# Revit family: Table-Teknion-CWRB_Reception_Communal_Bar-R2016
name_source: partatom
category: Furniture
revit_build: Autodesk Revit 2018 (Build: 20190510_1515(x64)
units: mm (PartAtom-declared; Revit-internal decimal feet)

## family parameters
Always vertical = Yes
Cut with Voids When Loaded = No
OmniClass Number = 23.40.20.00
OmniClass Title = General Furniture and Specialties
Room Calculation Point = No
Shared = Yes
Work Plane-Based = No

## types (4) — shared parameters
Assembly Code = E2020200
Manufacturer = Teknion
Manufacturer Fax = 416.661.4586
Part Number = CWRB
Product Documentation Link = https://assets.teknion.com
Product Line = Reception
Product Page URL = http://teknion.preprod.moveable.com
Series = Custom Wood
Sustainability Data = https://www.teknion.com
URL = www.teknion.com
Unit Weight URL = http://www.teknion.com
Warranty = http://www.teknion.com

## per-type parameters (varying)
| type | Center Unit Left Side Offset | Center Unit Right Side Offset | Description | LC | LEFT | LS | Model | RC | RIGHT | RS |
| Left Shelves End Storage | 28 " | 20 " | Teknion Reception, Communal Bar, 42" Depth, Left Shelf Storage | No | Yes | Yes | CWRB42_LS | No | No | No |
| Left Closed Cabinet End Storage | 28 " | 20 " | Teknion Reception, Communal Bar, 42" Depth, Left Closed Cabinet Storage | Yes | Yes | No | CWRB42_LC | No | No | No |
| Right Shelves End Storage | 20 " | 28 " | Teknion Reception, Communal Bar, 42" Depth, Right Shelf Storage | No | No | No | CWRB42_RS | No | Yes | Yes |
| Right Closed Cabinet End Storage | 20 " | 28 " | Teknion Reception, Communal Bar, 42" Depth, Right Closed Cabinet Storage | No | No | No | CWRB42_RC | Yes | Yes | No |

## geometry (parser evidence)
native form markers: Blend x29, Sweep x3
no freeform markers — native parametric forms only
